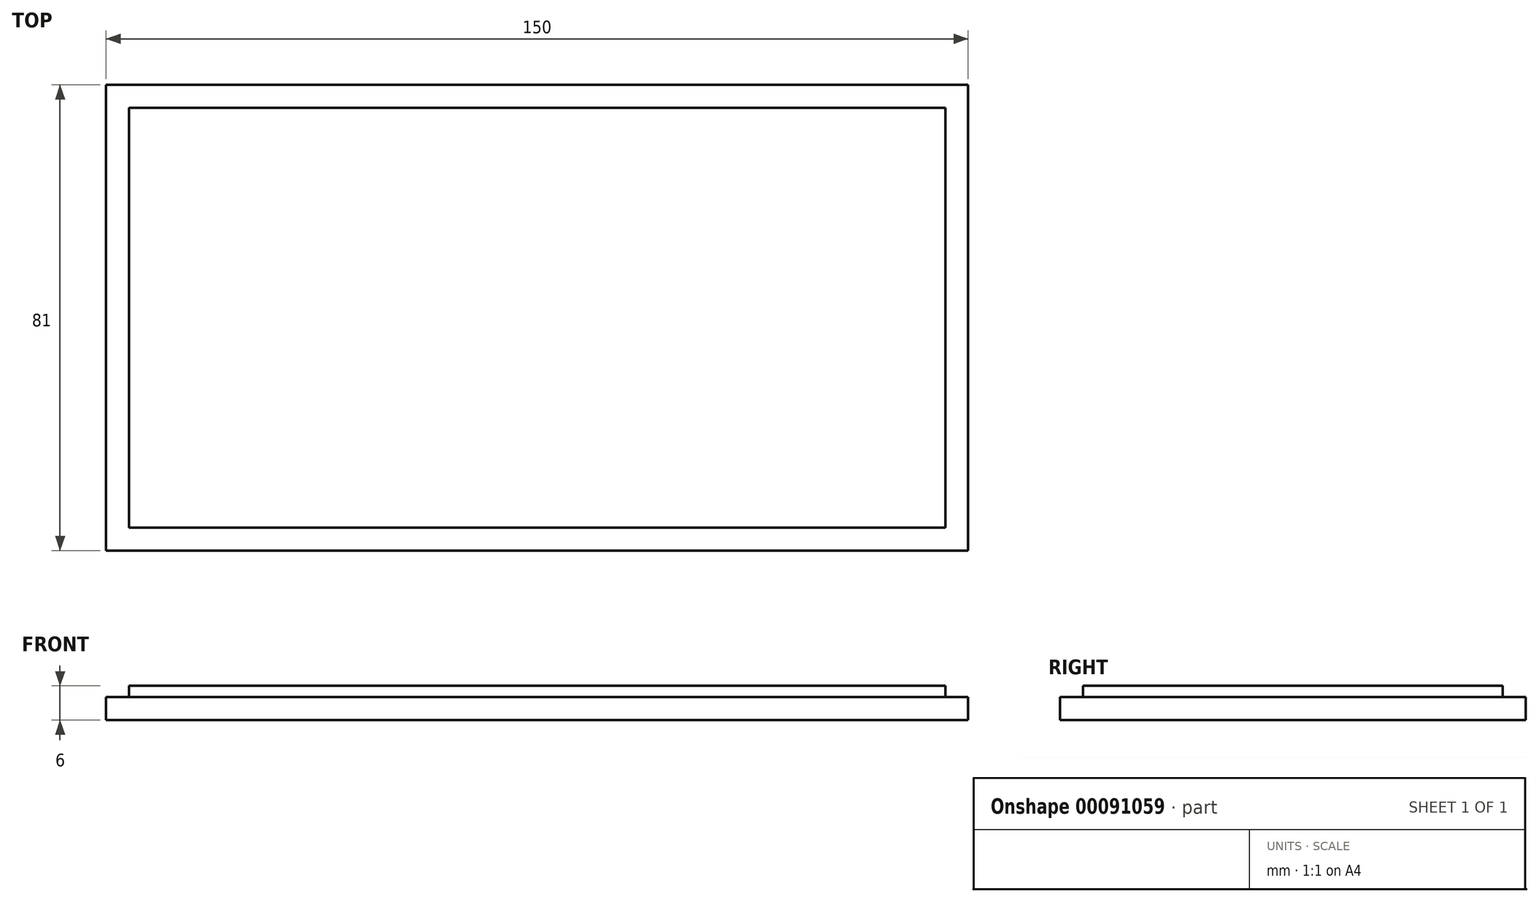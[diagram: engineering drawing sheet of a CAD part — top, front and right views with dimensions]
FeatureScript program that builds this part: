
annotation { "Feature Type Name" : "Feature", "Feature Type Description" : "" }
export const myFeature = defineFeature(function(context is Context, id is Id, definition is map)
    precondition{}
    {
        {
            var Q0;
            Q0=qCreatedBy(makeId("Top.planeOp"),FACE);
            var sketch = newSketch(context, id + "F0", { "sketchPlane" : qUnion([Q0])});
            skLineSegment(sketch, "E0.bottom", {"start": v(75, -40.5) * mm, "end": v(-75, -40.5) * mm});
            skLineSegment(sketch, "E0.top", {"start": v(75, 40.5) * mm, "end": v(-75, 40.5) * mm});
            skLineSegment(sketch, "E0.left", {"start": v(75, -40.5) * mm, "end": v(75, 40.5) * mm});
            skLineSegment(sketch, "E0.right", {"start": v(-75, -40.5) * mm, "end": v(-75, 40.5) * mm});
            skPoint(sketch, "E0.middle", {"position": v(0, 0) * mm});
            skSolve(sketch);
        }
        {
            var Q0;
            Q0=makeQuery(id+"F0.imprint","IMPRINT",FACE,{"disambiguationData":[TD([[makeQuery(id+"F0.imprint","IMPRINT",EDGE,{"derivedFrom":sQuery(id+"F0.wireOp",EDGE,"E0.bottom")}),-1.0]])]});
            extrude(context, id + "F1", {"entities" : qUnion([Q0]), "depth" : 6 * mm});
        }
        {
            var Q0;
            Q0=makeQuery(id+"F1.opExtrude","SWEPT_FACE",FACE,{"disambiguationData":[OSD([sQuery(id+"F0.wireOp",EDGE,"E0.bottom")])]});
            var sketch = newSketch(context, id + "F2", { "sketchPlane" : qUnion([Q0])});
            skLineSegment(sketch, "E1.bottom", {"start": v(-75, 6) * mm, "end": v(-71, 6) * mm});
            skLineSegment(sketch, "E1.top", {"start": v(-75, 4) * mm, "end": v(-71, 4) * mm});
            skLineSegment(sketch, "E1.left", {"start": v(-75, 6) * mm, "end": v(-75, 4) * mm});
            skLineSegment(sketch, "E1.right", {"start": v(-71, 6) * mm, "end": v(-71, 4) * mm});
            skSolve(sketch);
        }
        {
            var Q0;
            Q0=makeQuery(id+"F2.imprint","IMPRINT",FACE,{"disambiguationData":[TD([[makeQuery(id+"F2.imprint","IMPRINT",EDGE,{"derivedFrom":sQuery(id+"F2.wireOp",EDGE,"E1.bottom")}),1.0]])]});
            extrude(context, id + "F3", {"entities" : qUnion([Q0]), "operationType" : NewBodyOperationType.REMOVE, "oppositeDirection" : true, "depth" : 93 * mm});
        }
        {
            var Q0;
            Q0=makeQuery(id+"F1.opExtrude","SWEPT_FACE",FACE,{"disambiguationData":[OSD([sQuery(id+"F0.wireOp",EDGE,"E0.bottom")])]});
            var sketch = newSketch(context, id + "F4", { "sketchPlane" : qUnion([Q0])});
            skLineSegment(sketch, "E2.bottom", {"start": v(75, 6) * mm, "end": v(71, 6) * mm});
            skLineSegment(sketch, "E2.top", {"start": v(75, 4) * mm, "end": v(71, 4) * mm});
            skLineSegment(sketch, "E2.left", {"start": v(75, 6) * mm, "end": v(75, 4) * mm});
            skLineSegment(sketch, "E2.right", {"start": v(71, 6) * mm, "end": v(71, 4) * mm});
            skSolve(sketch);
        }
        {
            var Q0;
            Q0=makeQuery(id+"F4.imprint","IMPRINT",FACE,{"disambiguationData":[TD([[makeQuery(id+"F4.imprint","IMPRINT",EDGE,{"derivedFrom":sQuery(id+"F4.wireOp",EDGE,"E2.bottom")}),1.0]])]});
            extrude(context, id + "F5", {"entities" : qUnion([Q0]), "operationType" : NewBodyOperationType.REMOVE, "oppositeDirection" : true, "depth" : 93 * mm});
        }
        {
            var Q0;
            Q0=makeQuery(id+"F1.opExtrude","SWEPT_FACE",FACE,{"disambiguationData":[OSD([sQuery(id+"F0.wireOp",EDGE,"E0.bottom")])]});
            var sketch = newSketch(context, id + "F6", { "sketchPlane" : qUnion([Q0])});
            skLineSegment(sketch, "E3.bottom", {"start": v(-71, 6) * mm, "end": v(71, 6) * mm});
            skLineSegment(sketch, "E3.top", {"start": v(-71, 4) * mm, "end": v(71, 4) * mm});
            skLineSegment(sketch, "E3.left", {"start": v(-71, 6) * mm, "end": v(-71, 4) * mm});
            skLineSegment(sketch, "E3.right", {"start": v(71, 6) * mm, "end": v(71, 4) * mm});
            skSolve(sketch);
        }
        {
            var Q0;
            Q0=makeQuery(id+"F6.imprint","IMPRINT",FACE,{"disambiguationData":[TD([[makeQuery(id+"F6.imprint","IMPRINT",EDGE,{"derivedFrom":sQuery(id+"F6.wireOp",EDGE,"E3.bottom")}),1.0]])]});
            extrude(context, id + "F7", {"entities" : qUnion([Q0]), "operationType" : NewBodyOperationType.REMOVE, "oppositeDirection" : true, "depth" : 4 * mm});
        }
        {
            var Q0;
            Q0=makeQuery(id+"F1.opExtrude","SWEPT_FACE",FACE,{"disambiguationData":[OSD([sQuery(id+"F0.wireOp",EDGE,"E0.top")])]});
            var sketch = newSketch(context, id + "F8", { "sketchPlane" : qUnion([Q0])});
            skLineSegment(sketch, "E4.bottom", {"start": v(-71, 6) * mm, "end": v(71, 6) * mm});
            skLineSegment(sketch, "E4.top", {"start": v(-71, 4) * mm, "end": v(71, 4) * mm});
            skLineSegment(sketch, "E4.left", {"start": v(-71, 6) * mm, "end": v(-71, 4) * mm});
            skLineSegment(sketch, "E4.right", {"start": v(71, 6) * mm, "end": v(71, 4) * mm});
            skSolve(sketch);
        }
        {
            var Q0;
            Q0=makeQuery(id+"F8.imprint","IMPRINT",FACE,{"disambiguationData":[TD([[makeQuery(id+"F8.imprint","IMPRINT",EDGE,{"derivedFrom":sQuery(id+"F8.wireOp",EDGE,"E4.bottom")}),-1.0]])]});
            extrude(context, id + "F9", {"entities" : qUnion([Q0]), "operationType" : NewBodyOperationType.REMOVE, "oppositeDirection" : true, "depth" : 4 * mm});
        }
    });
